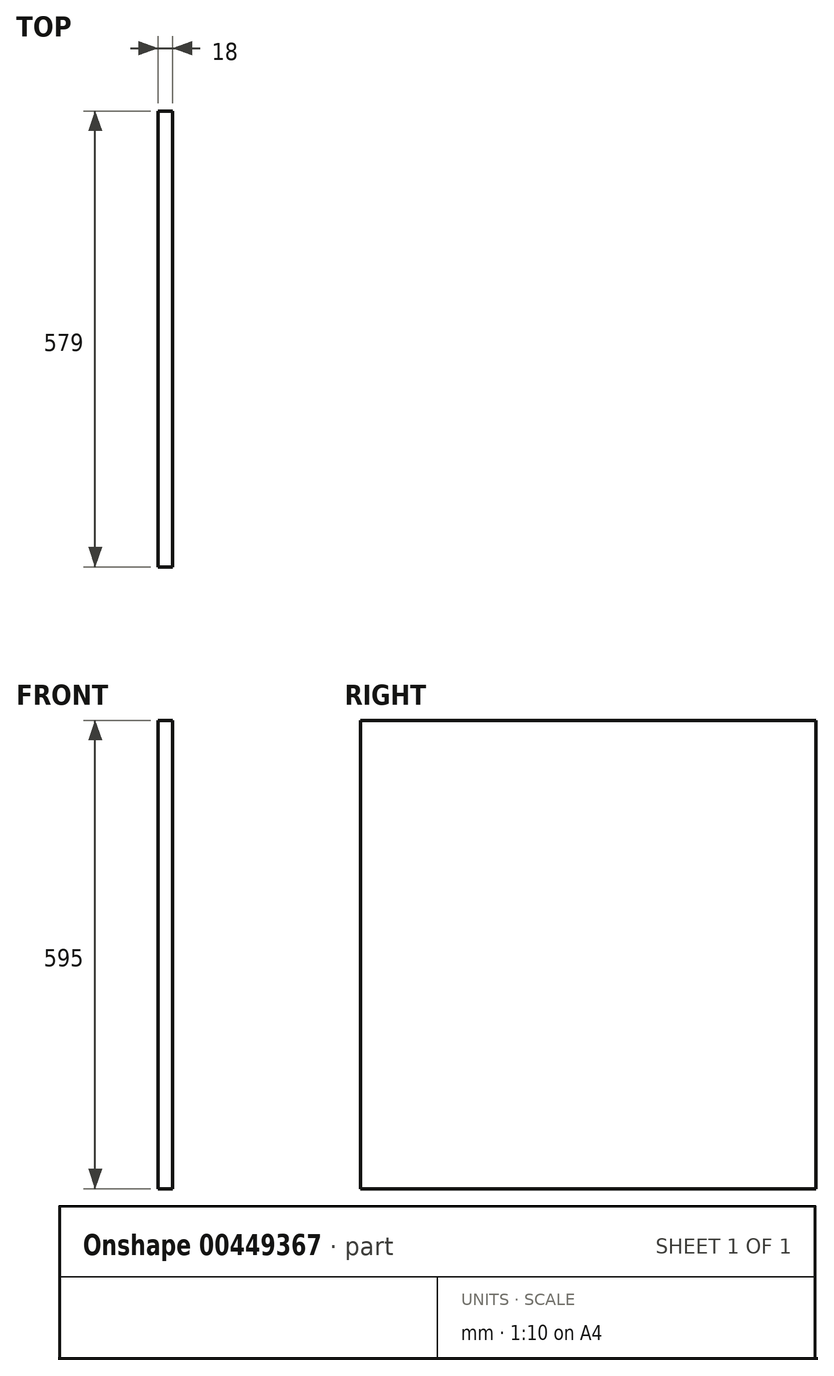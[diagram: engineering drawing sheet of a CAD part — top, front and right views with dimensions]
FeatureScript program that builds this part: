
annotation { "Feature Type Name" : "Feature", "Feature Type Description" : "" }
export const myFeature = defineFeature(function(context is Context, id is Id, definition is map)
    precondition{}
    {
        {
            var Q0;
            Q0=qCreatedBy(makeId("Right.planeOp"),FACE);
            var sketch = newSketch(context, id + "F0", { "sketchPlane" : qUnion([Q0])});
            skLineSegment(sketch, "E0.bottom", {"start": v(0, 695) * mm, "end": v(579, 695) * mm});
            skLineSegment(sketch, "E0.top", {"start": v(0, 100) * mm, "end": v(579, 100) * mm});
            skLineSegment(sketch, "E0.left", {"start": v(0, 695) * mm, "end": v(0, 100) * mm});
            skLineSegment(sketch, "E0.right", {"start": v(579, 695) * mm, "end": v(579, 100) * mm});
            skSolve(sketch);
        }
        {
            var Q0;
            Q0=qSketchRegion(id+"F0",true);
            extrude(context, id + "F1", {"entities" : qUnion([Q0]), "oppositeDirection" : true, "depth" : 18 * mm});
        }
    });
